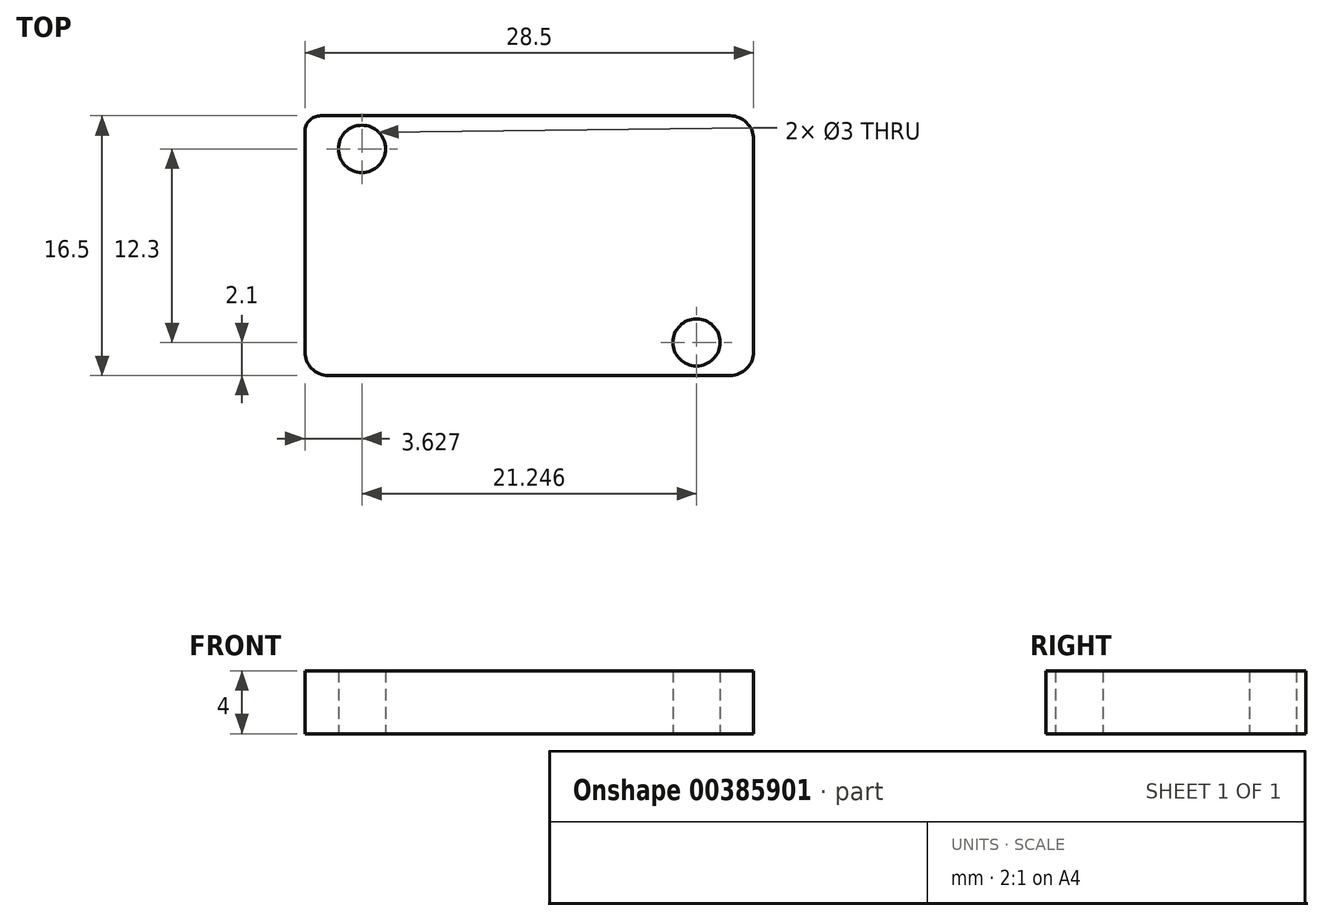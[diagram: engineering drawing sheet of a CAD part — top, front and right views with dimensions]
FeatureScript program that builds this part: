
annotation { "Feature Type Name" : "Feature", "Feature Type Description" : "" }
export const myFeature = defineFeature(function(context is Context, id is Id, definition is map)
    precondition{}
    {
        {
            var Q0;
            Q0=qCreatedBy(makeId("Top.planeOp"),FACE);
            var sketch = newSketch(context, id + "F0", { "sketchPlane" : qUnion([Q0])});
            skLineSegment(sketch, "E0.bottom", {"start": v(12.75, -8.25) * mm, "end": v(-12.75, -8.25) * mm});
            skLineSegment(sketch, "E0.top", {"start": v(12.75, 8.25) * mm, "end": v(-13.25, 8.25) * mm});
            skLineSegment(sketch, "E0.left", {"start": v(14.25, -6.75) * mm, "end": v(14.25, 6.75) * mm});
            skLineSegment(sketch, "E0.right", {"start": v(-14.25, -6.75) * mm, "end": v(-14.25, 7.25) * mm});
            skPoint(sketch, "E0.middle", {"position": v(0, 0) * mm});
            skLineSegment(sketch, "E1", {"start": v(-14.25, 8.25) * mm, "end": v(14.25, -8.25) * mm, "construction": true});
            skCircle(sketch, "E2", {"center": v(-10.62, 6.15) * mm, "radius": 1.5 * mm});
            skCircle(sketch, "E3", {"center": v(10.62, -6.15) * mm, "radius": 1.5 * mm});
            skPoint(sketch, "E4.visualSharp", {"position": v(-14.25, 8.25) * mm});
            skArc(sketch, "E4.filletArc", {"start": v(-13.25, 8.25) * mm, "mid": v(-13.96, 7.96) * mm, "end": v(-14.25, 7.25) * mm});
            skPoint(sketch, "E5.visualSharp", {"position": v(-14.25, -8.25) * mm});
            skArc(sketch, "E5.filletArc", {"start": v(-14.25, -6.75) * mm, "mid": v(-13.81, -7.81) * mm, "end": v(-12.75, -8.25) * mm});
            skPoint(sketch, "E6.visualSharp", {"position": v(14.25, -8.25) * mm});
            skArc(sketch, "E6.filletArc", {"start": v(12.75, -8.25) * mm, "mid": v(13.81, -7.81) * mm, "end": v(14.25, -6.75) * mm});
            skPoint(sketch, "E7.visualSharp", {"position": v(14.25, 8.25) * mm});
            skArc(sketch, "E7.filletArc", {"start": v(14.25, 6.75) * mm, "mid": v(13.81, 7.81) * mm, "end": v(12.75, 8.25) * mm});
            skSolve(sketch);
        }
        {
            var Q0;
            Q0=makeQuery(id+"F0.imprint","IMPRINT",FACE,{"disambiguationData":[TD([[makeQuery(id+"F0.imprint","IMPRINT",EDGE,{"derivedFrom":sQuery(id+"F0.wireOp",EDGE,"E0.bottom")}),-1.0]])]});
            extrude(context, id + "F1", {"entities" : qUnion([Q0]), "depth" : 4 * mm});
        }
    });
